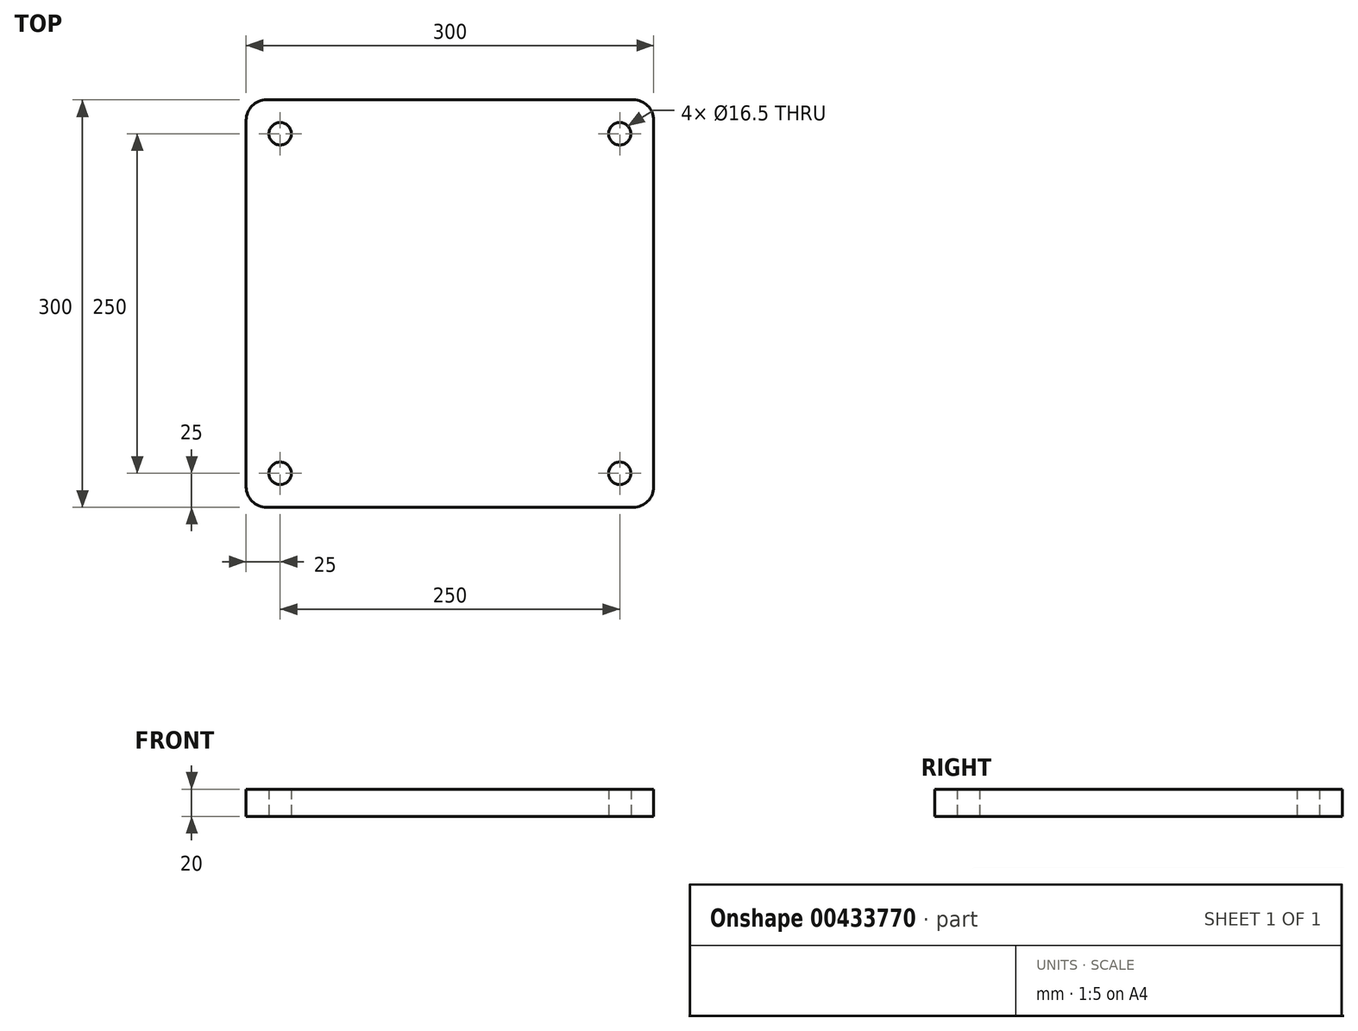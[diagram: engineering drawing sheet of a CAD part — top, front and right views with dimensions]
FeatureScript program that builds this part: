
annotation { "Feature Type Name" : "Feature", "Feature Type Description" : "" }
export const myFeature = defineFeature(function(context is Context, id is Id, definition is map)
    precondition{}
    {
        {
            var Q0;
            Q0=qCreatedBy(makeId("Top.planeOp"),FACE);
            var sketch = newSketch(context, id + "F0", { "sketchPlane" : qUnion([Q0])});
            skLineSegment(sketch, "E0.bottom", {"start": v(135, -150) * mm, "end": v(-135, -150) * mm});
            skLineSegment(sketch, "E0.top", {"start": v(135, 150) * mm, "end": v(-135, 150) * mm});
            skLineSegment(sketch, "E0.left", {"start": v(150, -135) * mm, "end": v(150, 135) * mm});
            skLineSegment(sketch, "E0.right", {"start": v(-150, -135) * mm, "end": v(-150, 135) * mm});
            skPoint(sketch, "E0.middle", {"position": v(0, 0) * mm});
            skPoint(sketch, "E1.visualSharp", {"position": v(-150, 150) * mm});
            skArc(sketch, "E1.filletArc", {"start": v(-135, 150) * mm, "mid": v(-145.6, 145.6) * mm, "end": v(-150, 135) * mm});
            skPoint(sketch, "E2.visualSharp", {"position": v(150, 150) * mm});
            skArc(sketch, "E2.filletArc", {"start": v(150, 135) * mm, "mid": v(145.6, 145.6) * mm, "end": v(135, 150) * mm});
            skPoint(sketch, "E3.visualSharp", {"position": v(150, -150) * mm});
            skArc(sketch, "E3.filletArc", {"start": v(135, -150) * mm, "mid": v(145.6, -145.6) * mm, "end": v(150, -135) * mm});
            skPoint(sketch, "E4.visualSharp", {"position": v(-150, -150) * mm});
            skArc(sketch, "E4.filletArc", {"start": v(-150, -135) * mm, "mid": v(-145.6, -145.6) * mm, "end": v(-135, -150) * mm});
            skLineSegment(sketch, "E5", {"start": v(-135, -135) * mm, "end": v(135, 135) * mm, "construction": true});
            skCircle(sketch, "E6", {"center": v(125, 125) * mm, "radius": 8.25 * mm});
            skCircle(sketch, "E7.1.1", {"center": v(-125, 125) * mm, "radius": 8.25 * mm});
            skCircle(sketch, "E7.2.1", {"center": v(-125, -125) * mm, "radius": 8.25 * mm});
            skCircle(sketch, "E7.3.1", {"center": v(125, -125) * mm, "radius": 8.25 * mm});
            skSolve(sketch);
        }
        {
            var Q0;
            Q0 = qSketchRegion(id + "F0", true);
            extrude(context, id + "F1", {"entities" : qUnion([Q0]), "depth" : 20 * mm});
        }
    });
